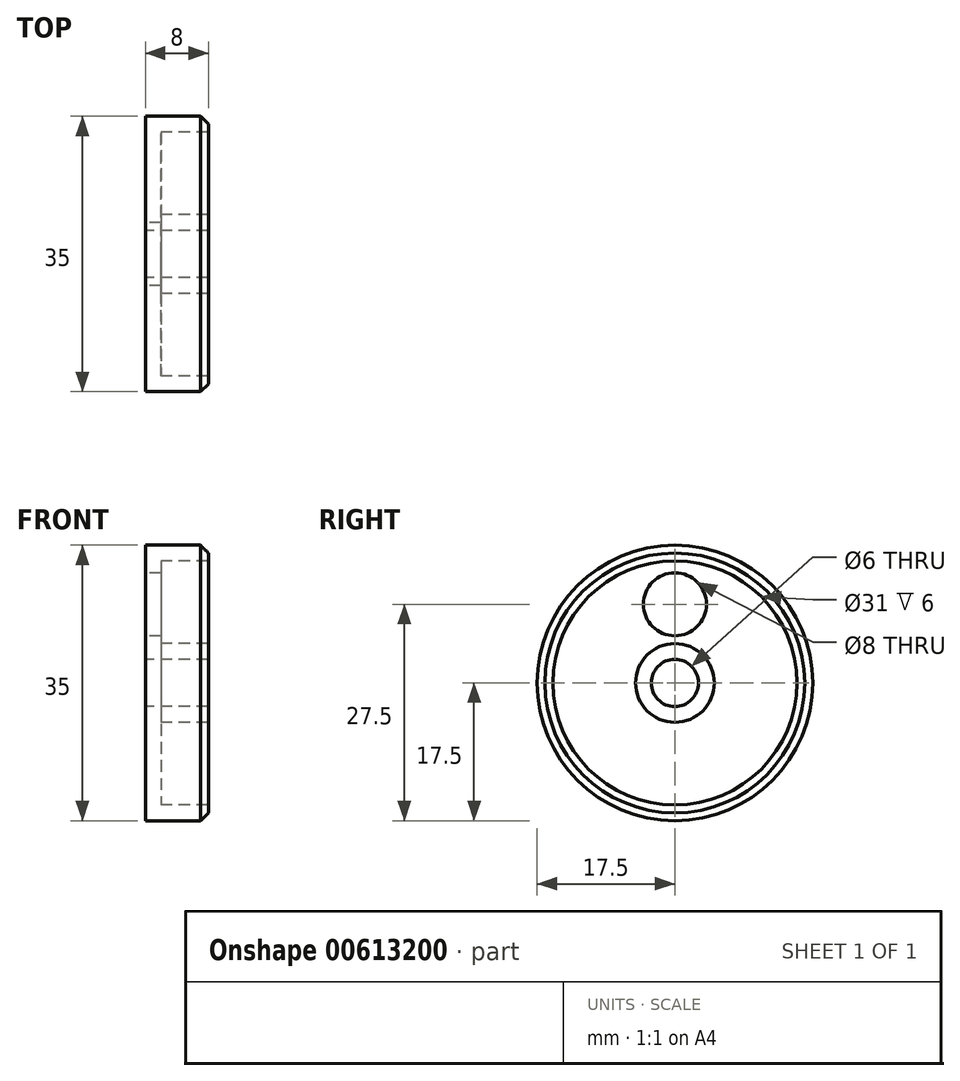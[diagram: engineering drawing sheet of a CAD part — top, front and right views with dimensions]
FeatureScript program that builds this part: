
annotation { "Feature Type Name" : "Feature", "Feature Type Description" : "" }
export const myFeature = defineFeature(function(context is Context, id is Id, definition is map)
    precondition{}
    {
        {
            var Q0;
            Q0=qCreatedBy(makeId("Front.planeOp"),FACE);
            var sketch = newSketch(context, id + "F0", { "sketchPlane" : qUnion([Q0])});
            skLineSegment(sketch, "E0.bottom", {"start": v(0, 0) * mm, "end": v(8, 0) * mm});
            skLineSegment(sketch, "E0.top", {"start": v(0, 17.5) * mm, "end": v(8, 17.5) * mm});
            skLineSegment(sketch, "E0.left", {"start": v(0, 0) * mm, "end": v(0, 17.5) * mm});
            skLineSegment(sketch, "E0.right", {"start": v(8, 0) * mm, "end": v(8, 17.5) * mm});
            skSolve(sketch);
        }
        {
            var Q0;
            Q0=makeQuery(id+"F0.imprint","IMPRINT",FACE,{"disambiguationData":[TD([[makeQuery(id+"F0.imprint","IMPRINT",EDGE,{"derivedFrom":sQuery(id+"F0.wireOp",EDGE,"E0.bottom")}),1.0]])]});
            var Q1;
            Q1=sQuery(id+"F0.wireOp",EDGE,"E0.bottom");
            revolve(context, id + "F1", {"entities" : qUnion([Q0]), "axis" : qUnion([Q1]), "revolveType" : RevolveType.ONE_DIRECTION, "angle" : 360 * degree});
        }
        {
            var Q0;
            Q0=qCreatedBy(makeId("Right.planeOp"),FACE);
            var sketch = newSketch(context, id + "F2", { "sketchPlane" : qUnion([Q0])});
            skPoint(sketch, "E1", {"position": v(0, 0) * mm});
            skSolve(sketch);
        }
        {
            var Q0;
            Q0=sQuery(id+"F2.wireOp",VERTEX,"E1");
            var Q1;
            Q1=makeQuery(id+"F1.opRevolve","SWEPT_BODY",BODY,{"disambiguationData":[OSD([sQuery(id+"F0.wireOp",EDGE,"E0.bottom"),sQuery(id+"F0.wireOp",EDGE,"E0.top"),sQuery(id+"F0.wireOp",EDGE,"E0.left"),sQuery(id+"F0.wireOp",EDGE,"E0.right")])]});
            hole(context, id + "F3", {"style" : HoleStyle.SIMPLE, "endStyle" : HoleEndStyle.THROUGH, "oppositeDirection" : true, "holeDiameter" : 6 * mm, "majorDiameter" : 5 * mm, "isTappedThrough" : true, "tappedDepth" : 12 * mm, "tapClearance" : 3, "locations" : qUnion([Q0]), "scope" : qUnion([Q1])});
        }
        {
            var Q0;
            Q0=makeQuery(id+"F1.opRevolve","SWEPT_FACE",FACE,{"disambiguationData":[OSD([sQuery(id+"F0.wireOp",EDGE,"E0.right")])]});
            var Q1;
            Q1=makeQuery(id+"F1.opRevolve","SWEPT_BODY",BODY,{"disambiguationData":[OSD([sQuery(id+"F0.wireOp",EDGE,"E0.bottom"),sQuery(id+"F0.wireOp",EDGE,"E0.top"),sQuery(id+"F0.wireOp",EDGE,"E0.left"),sQuery(id+"F0.wireOp",EDGE,"E0.right")])]});
            shell(context, id + "F4", {"entities" : qUnion([Q0]), "parts" : qUnion([Q1]), "thickness" : 2 * mm});
        }
        {
            var Q0;
            Q0=qCreatedBy(makeId("Right.planeOp"),FACE);
            var sketch = newSketch(context, id + "F5", { "sketchPlane" : qUnion([Q0])});
            skPoint(sketch, "E2", {"position": v(0, 10) * mm});
            skSolve(sketch);
        }
        {
            var Q0;
            Q0=sQuery(id+"F5.wireOp",VERTEX,"E2");
            var Q1;
            Q1=makeQuery(id+"F1.opRevolve","SWEPT_BODY",BODY,{"disambiguationData":[OSD([sQuery(id+"F0.wireOp",EDGE,"E0.bottom"),sQuery(id+"F0.wireOp",EDGE,"E0.top"),sQuery(id+"F0.wireOp",EDGE,"E0.left"),sQuery(id+"F0.wireOp",EDGE,"E0.right")])]});
            hole(context, id + "F6", {"style" : HoleStyle.SIMPLE, "endStyle" : HoleEndStyle.THROUGH, "oppositeDirection" : true, "holeDiameter" : 8 * mm, "majorDiameter" : 5 * mm, "isTappedThrough" : true, "tappedDepth" : 12 * mm, "tapClearance" : 3, "locations" : qUnion([Q0]), "scope" : qUnion([Q1])});
        }
        {
            var Q0;
            Q0=makeQuery(id+"F1.opRevolve","SWEPT_EDGE",EDGE,{"disambiguationData":[OSD([sQuery(id+"F0.wireOp",EDGE,"E0.top"),sQuery(id+"F0.wireOp",EDGE,"E0.right")])]});
            chamfer(context, id + "F7", {"entities" : qUnion([Q0]), "width" : 1 * mm, "tangentPropagation" : true});
        }
    });
